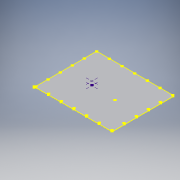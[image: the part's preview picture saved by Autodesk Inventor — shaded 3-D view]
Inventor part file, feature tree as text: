
AUTODESK INVENTOR PART (.ipt)
format: ipt  version: 2017 (Build 210142000, 142)  size: 201,216 bytes
history: native  units: in
note: dims shown in document units (in); Inventor stores cm internally (conversion verified against a paired STEP export)
features: sketch x5, hole x4, pattern_linear x4, extrude x1
ambient origin geometry x8: Origin, YZ Plane, XZ Plane, XY Plane, X Axis, Y Axis, Z Axis, Center Point
bodies: Solid1 (feature_tree)
feature tree (14):
  extrude  "Extrusion1"  Depth=8.0in
  sketch  "Sketch2"  dims[d4=0.06in d5=0.0in]
  hole  "Hole1"  [1 undecoded]
  pattern_linear  "Rectangular Pattern1"  Count1=7 Spacing1=1.635in
  pattern_linear  "Rectangular Pattern2"  Count1=5 Spacing1=1.562in
  hole  "Hole2"  [1 undecoded]
  pattern_linear  "Rectangular Pattern3"  Count1=5 Spacing1=1.562in
  pattern_linear  "Rectangular Pattern4"  Count1=7 Spacing1=1.635in
  sketch  "Sketch3"  dims[d6=0.096in d7=0.75in d8=0.16in d9=0.25in d10=0.5635in d11=1.0in d12=0.8108in d13=0.0935in]
  sketch  "Sketch6"  dims[d14=0.0935in d15=2.7559in d17=1.635in d18=1.9685in d20=1.562in]
  sketch  "Sketch7"  dims[d21=0.0935in d22=0.0935in d23=0.096in d24=0.75in d25=0.16in d26=0.25in d27=0.5635in d28=1.0in d29=0.8108in d30=1.9685in d32=1.562in d33=2.7559in d35=1.635in d36=0.128in d37=0.75in d38=0.232in d39=0.25in d40=0.5635in d41=0.06in d42=0.8108in d43=0.128in d44=0.75in d45=0.232in d46=0.25in d47=0.5635in d48=1.0in d49=0.8108in d50=4.344in d51=3.844in d52=3.062in d53=3.562in]
  hole  "Hole3"  [1 undecoded]
  hole  "Hole4"  [1 undecoded]
  sketch  "Sketch1"  dims[d0=10.0in d3=8.0in]
note: 4 required parameter values undecoded (feature->parameter linkage not recoverable at this tier; creation-order binding heuristic only, values carry confidence <= 0.55)
